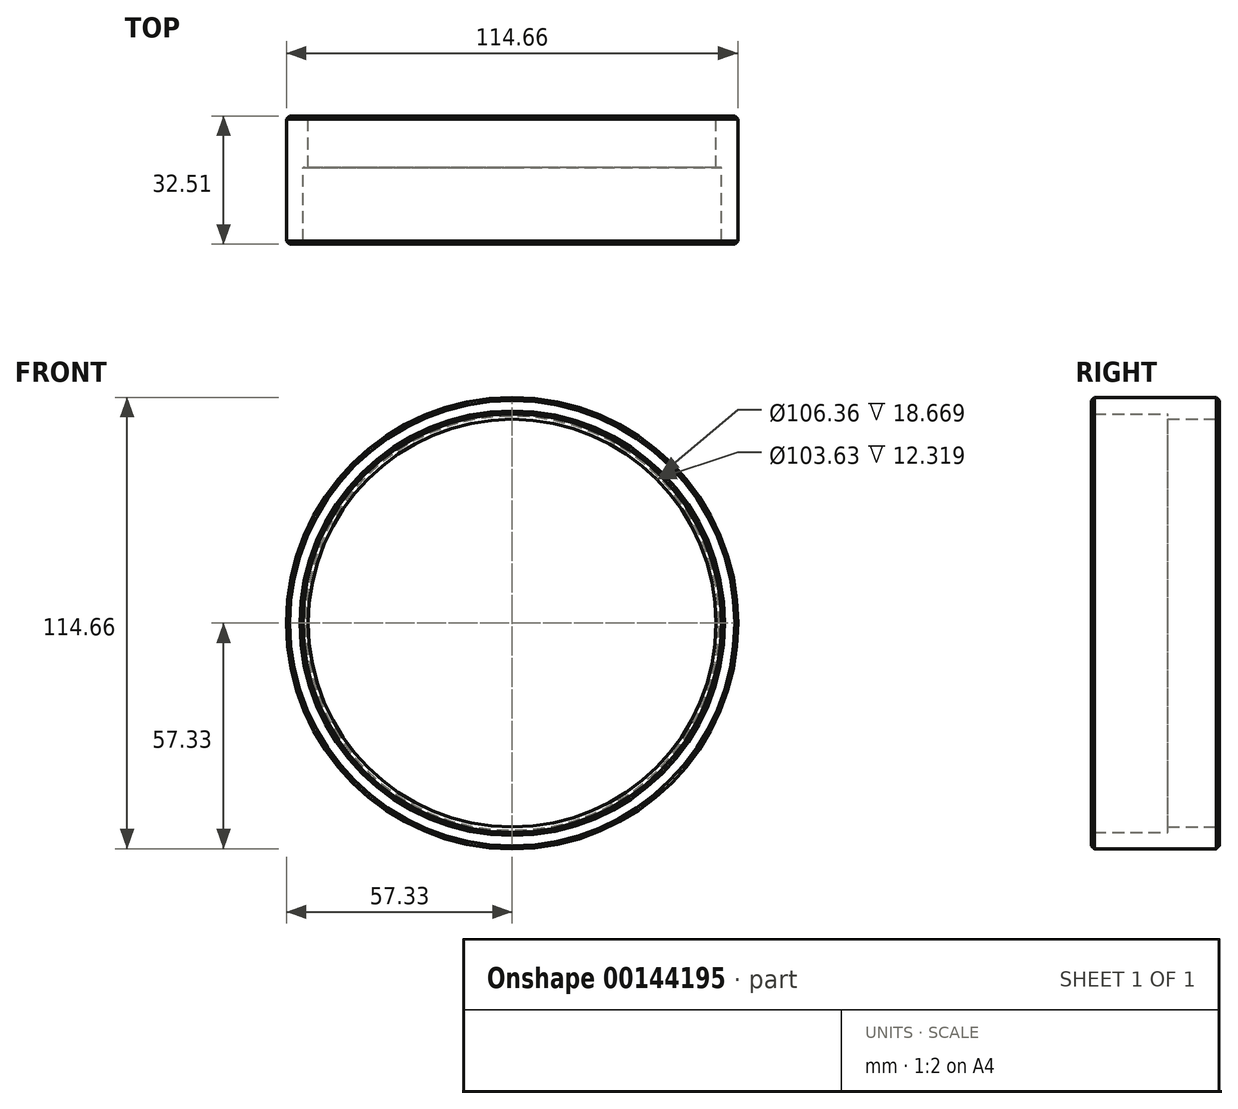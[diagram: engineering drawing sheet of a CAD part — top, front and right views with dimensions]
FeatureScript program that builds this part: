
annotation { "Feature Type Name" : "Feature", "Feature Type Description" : "" }
export const myFeature = defineFeature(function(context is Context, id is Id, definition is map)
    precondition{}
    {
        {
            var Q0;
            Q0=qCreatedBy(makeId("Front.planeOp"),FACE);
            var sketch = newSketch(context, id + "F0", { "sketchPlane" : qUnion([Q0])});
            skCircle(sketch, "E0", {"center": v(0, 0) * mm, "radius": 53.18 * mm});
            skCircle(sketch, "E1", {"center": v(0, 0) * mm, "radius": 57.33 * mm});
            skCircle(sketch, "E2", {"center": v(0, 0) * mm, "radius": 51.79 * mm});
            skSolve(sketch);
        }
        {
            var Q0;
            Q0=makeQuery(id+"F0.imprint","IMPRINT",FACE,{"disambiguationData":[TD([[makeQuery(id+"F0.imprint","IMPRINT",EDGE,{"derivedFrom":sQuery(id+"F0.wireOp",EDGE,"E0")}),-1.0]])]});
            extrude(context, id + "F1", {"entities" : qUnion([Q0]), "depth" : 32.5 * mm});
        }
        {
            var Q0;
            Q0=qCreatedBy(makeId("Front.planeOp"),FACE);
            var sketch = newSketch(context, id + "F2", { "sketchPlane" : qUnion([Q0])});
            skCircle(sketch, "E3", {"center": v(0, 0) * mm, "radius": 51.82 * mm});
            skCircle(sketch, "E4", {"center": v(0, 0) * mm, "radius": 53.4 * mm});
            skSolve(sketch);
        }
        {
            var Q0;
            Q0=makeQuery(id+"F2.imprint","IMPRINT",FACE,{"disambiguationData":[TD([[makeQuery(id+"F2.imprint","IMPRINT",EDGE,{"derivedFrom":sQuery(id+"F2.wireOp",EDGE,"E3")}),-1.0]])]});
            extrude(context, id + "F3", {"entities" : qUnion([Q0]), "operationType" : NewBodyOperationType.ADD, "depth" : 13.08 * mm});
        }
        {
            var Q0;
            Q0=makeQuery(id+"F1.opExtrude","CAP_EDGE",EDGE,{"disambiguationData":[OSD([sQuery(id+"F0.wireOp",EDGE,"E0")])],"isStart":false});
            var Q1;
            Q1=makeQuery(id+"F3.opExtrude","CAP_EDGE",EDGE,{"disambiguationData":[OSD([sQuery(id+"F2.wireOp",EDGE,"E3")])],"isStart":true});
            var Q2;
            Q2=makeQuery(id+"F1.opExtrude","CAP_EDGE",EDGE,{"disambiguationData":[OSD([sQuery(id+"F0.wireOp",EDGE,"E1")])],"isStart":false});
            var Q3;
            Q3=makeQuery(id+"F1.opExtrude","CAP_EDGE",EDGE,{"disambiguationData":[OSD([sQuery(id+"F0.wireOp",EDGE,"E1")])],"isStart":true});
            chamfer(context, id + "F4", {"entities" : qUnion([Q0, Q1, Q2, Q3]), "width" : 0.76 * mm, "tangentPropagation" : true});
        }
    });
